# Revit family: НЕВАТОМ_Вентилятор VKR, версия 1
name_source: partatom
category: Оборудование
revit_build: Autodesk Revit 2017 (Build: 20170118_1100(x64)
units: mm (PartAtom-declared; Revit-internal decimal feet)

## family parameters
Всегда вертикально = Да
На основе рабочей плоскости = Нет
Общий = Нет
При загрузке вырезать с полостями = Нет
Размер круглого соединителя = Использовать диаметр
Тип детали = Нормальный
Точка расчета площади = Нет

## types (9) — shared parameters
ADSK_Единица измерения = шт.
ADSK_Завод-изготовитель = НЕВАТОМ
ADSK_Количество = 1
ADSK_Материал наименование = Оцинкованная сталь
ADSK_Наименование = Вентилятор  крышный
ADSK_Расход воздуха = 0.0 м³/ч
Nevatom_URL = https://t.me
Ключевая пометка = Вентиляция
Материал = Сталь серая

## per-type parameters (varying)
| type | A | ADSK_Марка | ADSK_Масса | ADSK_Масса_Текст | ADSK_Напряжение | ADSK_Размер_Высота | ADSK_Размер_Длина | ADSK_Размер_Ширина | ADSK_Ток | ADSK_Частота вращения вентилятора | B | C | H | a | c | c2 | h | Макс. расход воздуха | Мощность двигателя N, кВт | Полное давление |
| VKR 300/22 - 2E | 300 мм | VKR 300/22 - 2E | 8.4 | 8,4 | 230 В | 255 мм | 380 мм | 380 мм | 1 А | 2600 | 380 мм | 223 мм | 255 мм | 240 мм | 152 мм | 28 мм | 32 мм | 1000.0 м³/ч | 0 кВт | 490.0 Па |
| VKR 900/63 - 4D | 900 мм | VKR 900/63 - 4D | 95.9 | 95.9 | 380 В | 522 мм | 1032 мм | 1032 мм | 7 А | 1370 | 1032 мм | 509 мм | 522 мм | 720 мм | 346 мм | 64 мм | 13 мм | 15000.0 м³/ч | 4 кВт | 900.0 Па |
| VKR 400/28 - 2E | 400 мм | VKR 400/28 - 2E | 12.1 | 12,1 | 230 В | 282 мм | 490 мм | 490 мм | 1 А | 2500 | 490 мм | 266 мм | 282 мм | 320 мм | 181 мм | 33 мм | 16 мм | 1800.0 м³/ч | 0 кВт | 600.0 Па |
| VKR 560/35 - 4E | 560 мм | VKR 560/35 - 4E | 24 | 24 | 230 В | 348 мм | 655 мм | 655 мм | 1 А | 1360 | 655 мм | 332 мм | 348 мм | 448 мм | 226 мм | 42 мм | 16 мм | 2200.0 м³/ч | 0 кВт | 260.0 Па |
| VKR 560/35 - 4D | 560 мм | VKR 560/35 - 4D | 24 | 24 | 380 В | 348 мм | 655 мм | 655 мм | 0 А | 1380 | 655 мм | 332 мм | 348 мм | 448 мм | 226 мм | 42 мм | 16 мм | 2500.0 м³/ч | 0 кВт | 300.0 Па |
| VKR 560/40 - 4E | 560 мм | VKR 560/40 - 4E | 27.8 | 27,8 | 230 В | 350 мм | 655 мм | 655 мм | 2 А | 1350 | 655 мм | 333 мм | 350 мм | 448 мм | 226 мм | 42 мм | 17 мм | 4000.0 м³/ч | 1 кВт | 480.0 Па |
| VKR 630/45 - 4E | 630 мм | VKR 630/45 - 4E | 36.2 | 36,2 | 230 В | 429 мм | 775 мм | 775 мм | 4 А | 1340 | 775 мм | 414 мм | 429 мм | 504 мм | 282 мм | 52 мм | 15 мм | 6000.0 м³/ч | 1 кВт | 450.0 Па |
| VKR 630/50 - 4D | 630 мм | VKR 630/45 - 4E | 45.8 | 45,8 | 380 В | 443 мм | 775 мм | 775 мм | 3 А | 1330 | 775 мм | 430 мм | 443 мм | 504 мм | 292 мм | 54 мм | 13 мм | 8000.0 м³/ч | 2 кВт | 530.0 Па |
| VKR 900/56 - 4D | 900 мм | VKR 900/56 - 4D | 71.4 | 71,4 | 380 В | 475 мм | 1015 мм | 1015 мм | 4 А | 1325 | 1015 мм | 461 мм | 475 мм | 720 мм | 313 мм | 58 мм | 14 мм | 10000.0 м³/ч | 2 кВт | 700.0 Па |
